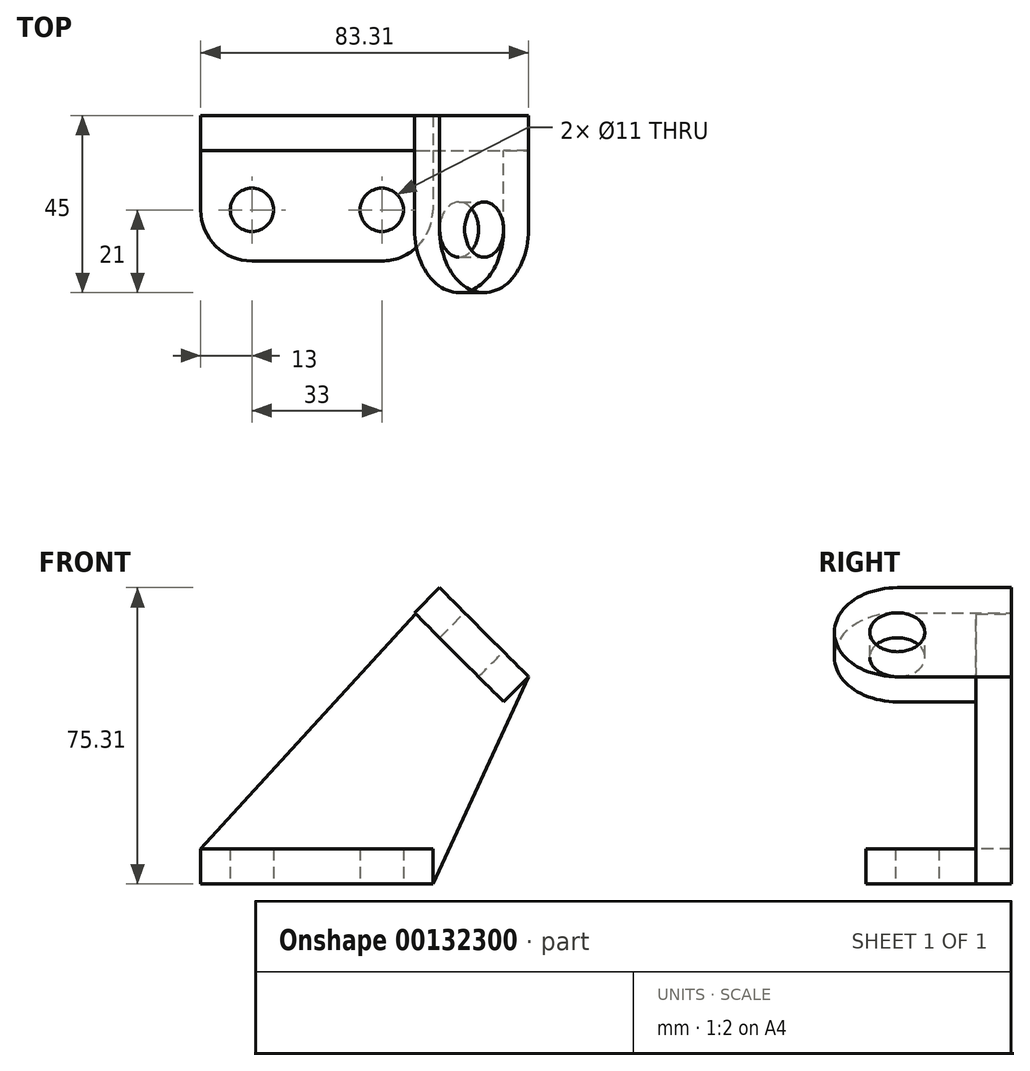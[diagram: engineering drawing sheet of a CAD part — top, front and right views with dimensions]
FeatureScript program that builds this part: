
annotation { "Feature Type Name" : "Feature", "Feature Type Description" : "" }
export const myFeature = defineFeature(function(context is Context, id is Id, definition is map)
    precondition{}
    {
        {
            var Q0;
            Q0=qCreatedBy(makeId("Top.planeOp"),FACE);
            var sketch = newSketch(context, id + "F0", { "sketchPlane" : qUnion([Q0])});
            skLineSegment(sketch, "E0.bottom", {"start": v(0, 0) * mm, "end": v(59, 0) * mm});
            skLineSegment(sketch, "E0.top", {"start": v(13, -37) * mm, "end": v(46, -37) * mm});
            skLineSegment(sketch, "E0.left", {"start": v(0, 0) * mm, "end": v(0, -24) * mm});
            skLineSegment(sketch, "E0.right", {"start": v(59, 0) * mm, "end": v(59, -24) * mm});
            skCircle(sketch, "E1", {"center": v(13, -24) * mm, "radius": 5.5 * mm});
            skCircle(sketch, "E2", {"center": v(46, -24) * mm, "radius": 5.5 * mm});
            skPoint(sketch, "E3.visualSharp", {"position": v(59, -37) * mm});
            skArc(sketch, "E3.filletArc", {"start": v(46, -37) * mm, "mid": v(55.2, -33.2) * mm, "end": v(59, -24) * mm});
            skPoint(sketch, "E4.visualSharp", {"position": v(0, -37) * mm});
            skArc(sketch, "E4.filletArc", {"start": v(0, -24) * mm, "mid": v(3.8, -33.2) * mm, "end": v(13, -37) * mm});
            skSolve(sketch);
        }
        {
            var Q0;
            Q0=makeQuery(id+"F0.imprint","IMPRINT",FACE,{"disambiguationData":[TD([[makeQuery(id+"F0.imprint","IMPRINT",EDGE,{"derivedFrom":sQuery(id+"F0.wireOp",EDGE,"E0.bottom")}),-1.0]])]});
            extrude(context, id + "F1", {"entities" : qUnion([Q0]), "depth" : 9 * mm});
        }
        {
            var Q0;
            Q0=makeQuery(id+"F1.opExtrude","SWEPT_FACE",FACE,{"disambiguationData":[OSD([sQuery(id+"F0.wireOp",EDGE,"E0.bottom")])]});
            var sketch = newSketch(context, id + "F2", { "sketchPlane" : qUnion([Q0])});
            skLineSegment(sketch, "E5", {"start": v(0, 9) * mm, "end": v(-60.69, 75.31) * mm});
            skLineSegment(sketch, "E6", {"start": v(-59, 0) * mm, "end": v(-83.31, 52.69) * mm});
            skLineSegment(sketch, "E7", {"start": v(-60.69, 75.31) * mm, "end": v(-83.31, 52.69) * mm});
            skPoint(sketch, "E8", {"position": v(-72, 64) * mm});
            skLineSegment(sketch, "E9", {"start": v(-72, 64) * mm, "end": v(-94.93, 64) * mm, "construction": true});
            skSolve(sketch);
        }
        {
            var Q0;
            Q0 = qSketchRegion(id + "F2", true);
            var Q1;
            Q1=makeQuery(id+"F2.imprint","IMPRINT",FACE,{"disambiguationData":[TD([[makeQuery(id+"F2.imprint","IMPRINT",EDGE,{"derivedFrom":sQuery(id+"F2.wireOp",EDGE,"E5")}),1.0]])]});
            extrude(context, id + "F3", {"entities" : qUnion([Q0, Q1]), "operationType" : NewBodyOperationType.ADD, "oppositeDirection" : true, "depth" : 9 * mm});
        }
        {
            var Q0;
            Q0=makeQuery(id+"F3.opExtrude","SWEPT_FACE",FACE,{"disambiguationData":[OSD([sQuery(id+"F2.wireOp",EDGE,"E7")])]});
            var sketch = newSketch(context, id + "F4", { "sketchPlane" : qUnion([Q0])});
            skLineSegment(sketch, "E10.0.0", {"start": v(0, -21.66) * mm, "end": v(0, 10.34) * mm});
            skLineSegment(sketch, "E11", {"start": v(0, 10.34) * mm, "end": v(-29, 10.34) * mm});
            skLineSegment(sketch, "E12", {"start": v(0, -21.66) * mm, "end": v(-29, -21.66) * mm});
            skPoint(sketch, "E12.endSnap0", {"position": v(-4.5, -21.66) * mm});
            skArc(sketch, "E13", {"start": v(-29, 10.34) * mm, "mid": v(-45, -5.66) * mm, "end": v(-29, -21.66) * mm});
            skPoint(sketch, "E13.centerSnap0", {"position": v(-9, -5.66) * mm});
            skCircle(sketch, "E14", {"center": v(-29, -5.66) * mm, "radius": 7 * mm});
            skSolve(sketch);
        }
        {
            var Q0;
            Q0 = qSketchRegion(id + "F4", true);
            extrude(context, id + "F5", {"entities" : qUnion([Q0]), "operationType" : NewBodyOperationType.ADD, "oppositeDirection" : true, "depth" : 9 * mm});
        }
    });
